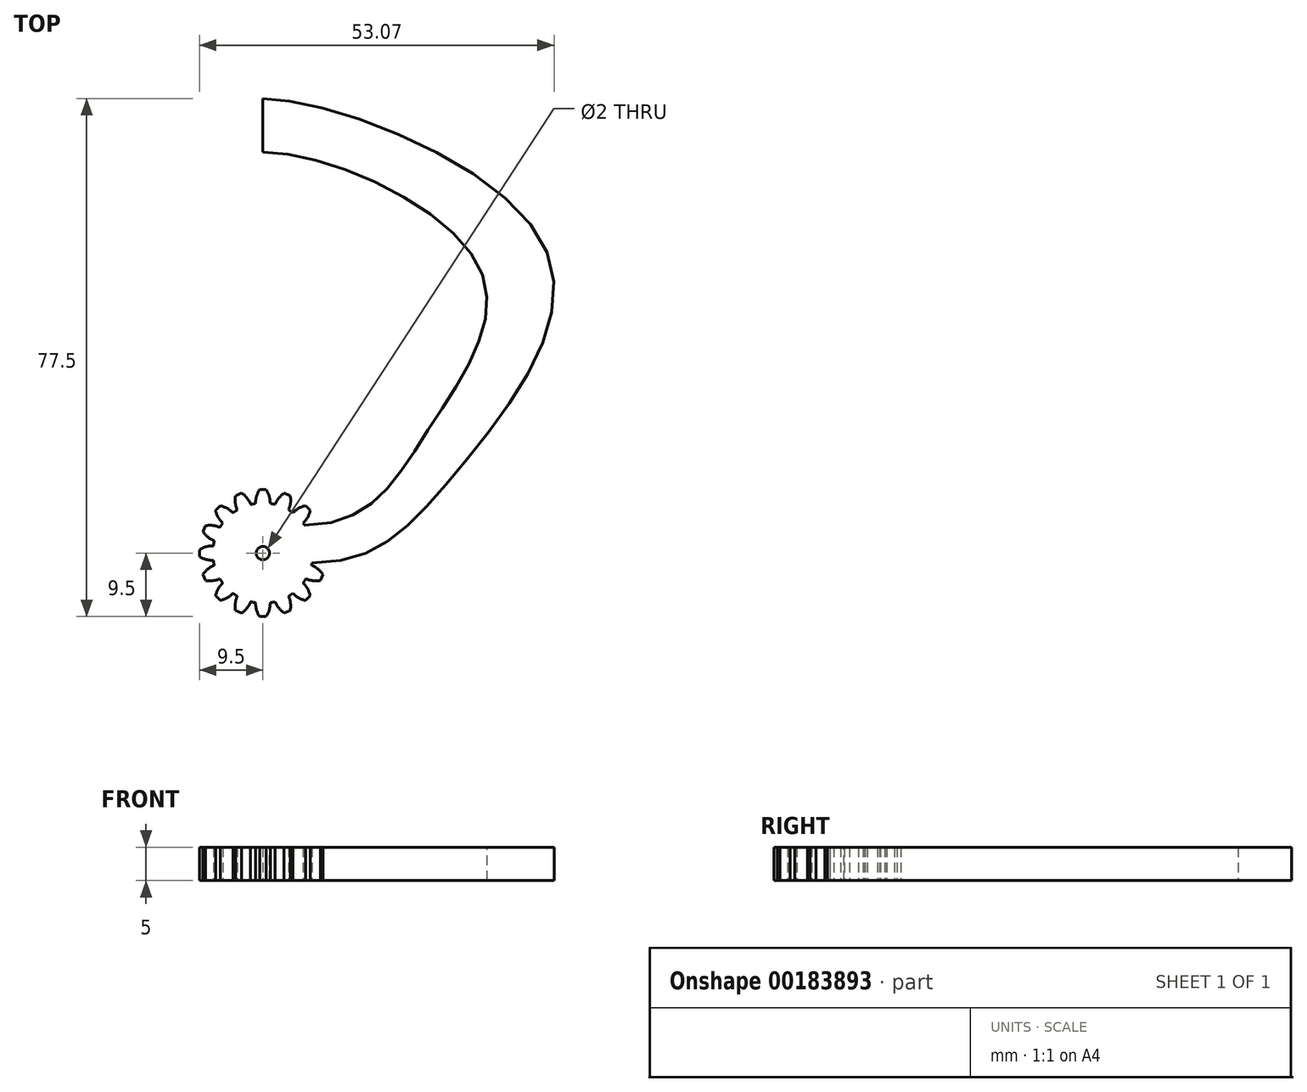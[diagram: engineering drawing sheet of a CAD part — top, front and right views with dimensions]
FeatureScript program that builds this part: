
annotation { "Feature Type Name" : "Feature", "Feature Type Description" : "" }
export const myFeature = defineFeature(function(context is Context, id is Id, definition is map)
    precondition{}
    {
        {
            var Q0;
            Q0=qCreatedBy(makeId("Top.planeOp"),FACE);
            var sketch = newSketch(context, id + "F0", { "sketchPlane" : qUnion([Q0])});
            skCircle(sketch, "E0", {"center": v(0, 0) * mm, "radius": 7.5 * mm});
            skLineSegment(sketch, "E1", {"start": v(0, 0) * mm, "end": v(0, 7.5) * mm, "construction": true});
            skLineSegment(sketch, "E2", {"start": v(0, 9.5) * mm, "end": v(-0.5, 9.5) * mm});
            skArc(sketch, "E3", {"start": v(-0.5, 9.5) * mm, "mid": v(-0.95, 8.5) * mm, "end": v(-1.09, 7.42) * mm});
            skLineSegment(sketch, "E4.MirrorCS", {"start": v(0, 9.5) * mm, "end": v(0.5, 9.5) * mm});
            skArc(sketch, "E5.MirrorCS", {"start": v(0.5, 9.5) * mm, "mid": v(0.95, 8.5) * mm, "end": v(1.09, 7.42) * mm});
            skLineSegment(sketch, "E6.1.0", {"start": v(-3.64, 8.78) * mm, "end": v(-4.1, 8.59) * mm});
            skArc(sketch, "E6.1.1", {"start": v(-4.1, 8.59) * mm, "mid": v(-4.13, 7.5) * mm, "end": v(-3.85, 6.44) * mm});
            skLineSegment(sketch, "E6.1.2", {"start": v(-3.64, 8.78) * mm, "end": v(-3.17, 8.97) * mm});
            skArc(sketch, "E6.1.3", {"start": v(-3.17, 8.97) * mm, "mid": v(-2.38, 8.22) * mm, "end": v(-1.83, 7.27) * mm});
            skLineSegment(sketch, "E6.2.0", {"start": v(-6.72, 6.72) * mm, "end": v(-7.07, 6.36) * mm});
            skArc(sketch, "E6.2.1", {"start": v(-7.07, 6.36) * mm, "mid": v(-6.69, 5.34) * mm, "end": v(-6.02, 4.48) * mm});
            skLineSegment(sketch, "E6.2.2", {"start": v(-6.72, 6.72) * mm, "end": v(-6.36, 7.07) * mm});
            skArc(sketch, "E6.2.3", {"start": v(-6.36, 7.07) * mm, "mid": v(-5.34, 6.69) * mm, "end": v(-4.48, 6.02) * mm});
            skLineSegment(sketch, "E6.3.0", {"start": v(-8.78, 3.64) * mm, "end": v(-8.97, 3.17) * mm});
            skArc(sketch, "E6.3.1", {"start": v(-8.97, 3.17) * mm, "mid": v(-8.22, 2.38) * mm, "end": v(-7.27, 1.83) * mm});
            skLineSegment(sketch, "E6.3.2", {"start": v(-8.78, 3.64) * mm, "end": v(-8.59, 4.1) * mm});
            skArc(sketch, "E6.3.3", {"start": v(-8.59, 4.1) * mm, "mid": v(-7.5, 4.13) * mm, "end": v(-6.44, 3.85) * mm});
            skLineSegment(sketch, "E6.4.0", {"start": v(-9.5, 0) * mm, "end": v(-9.5, -0.5) * mm});
            skArc(sketch, "E6.4.1", {"start": v(-9.5, -0.5) * mm, "mid": v(-8.5, -0.95) * mm, "end": v(-7.42, -1.09) * mm});
            skLineSegment(sketch, "E6.4.2", {"start": v(-9.5, 0) * mm, "end": v(-9.5, 0.5) * mm});
            skArc(sketch, "E6.4.3", {"start": v(-9.5, 0.5) * mm, "mid": v(-8.5, 0.95) * mm, "end": v(-7.42, 1.09) * mm});
            skLineSegment(sketch, "E6.5.0", {"start": v(-8.78, -3.64) * mm, "end": v(-8.59, -4.1) * mm});
            skArc(sketch, "E6.5.1", {"start": v(-8.59, -4.1) * mm, "mid": v(-7.5, -4.13) * mm, "end": v(-6.44, -3.85) * mm});
            skLineSegment(sketch, "E6.5.2", {"start": v(-8.78, -3.64) * mm, "end": v(-8.97, -3.17) * mm});
            skArc(sketch, "E6.5.3", {"start": v(-8.97, -3.17) * mm, "mid": v(-8.22, -2.38) * mm, "end": v(-7.27, -1.83) * mm});
            skLineSegment(sketch, "E6.6.0", {"start": v(-6.72, -6.72) * mm, "end": v(-6.36, -7.07) * mm});
            skArc(sketch, "E6.6.1", {"start": v(-6.36, -7.07) * mm, "mid": v(-5.34, -6.69) * mm, "end": v(-4.48, -6.02) * mm});
            skLineSegment(sketch, "E6.6.2", {"start": v(-6.72, -6.72) * mm, "end": v(-7.07, -6.36) * mm});
            skArc(sketch, "E6.6.3", {"start": v(-7.07, -6.36) * mm, "mid": v(-6.69, -5.34) * mm, "end": v(-6.02, -4.48) * mm});
            skLineSegment(sketch, "E6.7.0", {"start": v(-3.64, -8.78) * mm, "end": v(-3.17, -8.97) * mm});
            skArc(sketch, "E6.7.1", {"start": v(-3.17, -8.97) * mm, "mid": v(-2.38, -8.22) * mm, "end": v(-1.83, -7.27) * mm});
            skLineSegment(sketch, "E6.7.2", {"start": v(-3.64, -8.78) * mm, "end": v(-4.1, -8.59) * mm});
            skArc(sketch, "E6.7.3", {"start": v(-4.1, -8.59) * mm, "mid": v(-4.13, -7.5) * mm, "end": v(-3.85, -6.44) * mm});
            skLineSegment(sketch, "E6.8.0", {"start": v(0, -9.5) * mm, "end": v(0.5, -9.5) * mm});
            skArc(sketch, "E6.8.1", {"start": v(0.5, -9.5) * mm, "mid": v(0.95, -8.5) * mm, "end": v(1.09, -7.42) * mm});
            skLineSegment(sketch, "E6.8.2", {"start": v(0, -9.5) * mm, "end": v(-0.5, -9.5) * mm});
            skArc(sketch, "E6.8.3", {"start": v(-0.5, -9.5) * mm, "mid": v(-0.95, -8.5) * mm, "end": v(-1.09, -7.42) * mm});
            skLineSegment(sketch, "E6.9.0", {"start": v(3.64, -8.78) * mm, "end": v(4.1, -8.59) * mm});
            skArc(sketch, "E6.9.1", {"start": v(4.1, -8.59) * mm, "mid": v(4.13, -7.5) * mm, "end": v(3.85, -6.44) * mm});
            skLineSegment(sketch, "E6.9.2", {"start": v(3.64, -8.78) * mm, "end": v(3.17, -8.97) * mm});
            skArc(sketch, "E6.9.3", {"start": v(3.17, -8.97) * mm, "mid": v(2.38, -8.22) * mm, "end": v(1.83, -7.27) * mm});
            skLineSegment(sketch, "E6.10.0", {"start": v(6.72, -6.72) * mm, "end": v(7.07, -6.36) * mm});
            skArc(sketch, "E6.10.1", {"start": v(7.07, -6.36) * mm, "mid": v(6.69, -5.34) * mm, "end": v(6.02, -4.48) * mm});
            skLineSegment(sketch, "E6.10.2", {"start": v(6.72, -6.72) * mm, "end": v(6.36, -7.07) * mm});
            skArc(sketch, "E6.10.3", {"start": v(6.36, -7.07) * mm, "mid": v(5.34, -6.69) * mm, "end": v(4.48, -6.02) * mm});
            skLineSegment(sketch, "E6.11.0", {"start": v(8.78, -3.64) * mm, "end": v(8.97, -3.17) * mm});
            skArc(sketch, "E6.11.1", {"start": v(8.97, -3.17) * mm, "mid": v(8.22, -2.38) * mm, "end": v(7.27, -1.83) * mm});
            skLineSegment(sketch, "E6.11.2", {"start": v(8.78, -3.64) * mm, "end": v(8.59, -4.1) * mm});
            skArc(sketch, "E6.11.3", {"start": v(8.59, -4.1) * mm, "mid": v(7.5, -4.13) * mm, "end": v(6.44, -3.85) * mm});
            skLineSegment(sketch, "E6.12.0", {"start": v(9.5, 0) * mm, "end": v(9.5, 0.5) * mm});
            skArc(sketch, "E6.12.1", {"start": v(9.5, 0.5) * mm, "mid": v(8.5, 0.95) * mm, "end": v(7.42, 1.09) * mm});
            skLineSegment(sketch, "E6.12.2", {"start": v(9.5, 0) * mm, "end": v(9.5, -0.5) * mm});
            skArc(sketch, "E6.12.3", {"start": v(9.5, -0.5) * mm, "mid": v(8.5, -0.95) * mm, "end": v(7.42, -1.09) * mm});
            skLineSegment(sketch, "E6.13.0", {"start": v(8.78, 3.64) * mm, "end": v(8.59, 4.1) * mm});
            skArc(sketch, "E6.13.1", {"start": v(8.59, 4.1) * mm, "mid": v(7.5, 4.13) * mm, "end": v(6.44, 3.85) * mm});
            skLineSegment(sketch, "E6.13.2", {"start": v(8.78, 3.64) * mm, "end": v(8.97, 3.17) * mm});
            skArc(sketch, "E6.13.3", {"start": v(8.97, 3.17) * mm, "mid": v(8.22, 2.38) * mm, "end": v(7.27, 1.83) * mm});
            skLineSegment(sketch, "E6.14.0", {"start": v(6.72, 6.72) * mm, "end": v(6.36, 7.07) * mm});
            skArc(sketch, "E6.14.1", {"start": v(6.36, 7.07) * mm, "mid": v(5.34, 6.69) * mm, "end": v(4.48, 6.02) * mm});
            skLineSegment(sketch, "E6.14.2", {"start": v(6.72, 6.72) * mm, "end": v(7.07, 6.36) * mm});
            skArc(sketch, "E6.14.3", {"start": v(7.07, 6.36) * mm, "mid": v(6.69, 5.34) * mm, "end": v(6.02, 4.48) * mm});
            skLineSegment(sketch, "E6.15.0", {"start": v(3.64, 8.78) * mm, "end": v(3.17, 8.97) * mm});
            skArc(sketch, "E6.15.1", {"start": v(3.17, 8.97) * mm, "mid": v(2.38, 8.22) * mm, "end": v(1.83, 7.27) * mm});
            skLineSegment(sketch, "E6.15.2", {"start": v(3.64, 8.78) * mm, "end": v(4.1, 8.59) * mm});
            skArc(sketch, "E6.15.3", {"start": v(4.1, 8.59) * mm, "mid": v(4.13, 7.5) * mm, "end": v(3.85, 6.44) * mm});
            skSolve(sketch);
        }
        {
            var Q0;
            Q0=qSketchRegion(id+"F0",true);
            extrude(context, id + "F1", {"entities" : qUnion([Q0]), "depth" : 5 * mm});
        }
        {
            var Q0;
            Q0=makeQuery(id+"F1.opExtrude","CAP_FACE",FACE,{"disambiguationData":[OSD([sQuery(id+"F0.wireOp",EDGE,"E0"),sQuery(id+"F0.wireOp",EDGE,"E2"),sQuery(id+"F0.wireOp",EDGE,"E3"),sQuery(id+"F0.wireOp",EDGE,"E4.MirrorCS"),sQuery(id+"F0.wireOp",EDGE,"E5.MirrorCS"),sQuery(id+"F0.wireOp",EDGE,"E6.1.0"),sQuery(id+"F0.wireOp",EDGE,"E6.1.1"),sQuery(id+"F0.wireOp",EDGE,"E6.1.2"),sQuery(id+"F0.wireOp",EDGE,"E6.1.3"),sQuery(id+"F0.wireOp",EDGE,"E6.2.0"),sQuery(id+"F0.wireOp",EDGE,"E6.2.1"),sQuery(id+"F0.wireOp",EDGE,"E6.2.2"),sQuery(id+"F0.wireOp",EDGE,"E6.2.3"),sQuery(id+"F0.wireOp",EDGE,"E6.3.0"),sQuery(id+"F0.wireOp",EDGE,"E6.3.1"),sQuery(id+"F0.wireOp",EDGE,"E6.3.2"),sQuery(id+"F0.wireOp",EDGE,"E6.3.3"),sQuery(id+"F0.wireOp",EDGE,"E6.4.0"),sQuery(id+"F0.wireOp",EDGE,"E6.4.1"),sQuery(id+"F0.wireOp",EDGE,"E6.4.2"),sQuery(id+"F0.wireOp",EDGE,"E6.4.3"),sQuery(id+"F0.wireOp",EDGE,"E6.5.0"),sQuery(id+"F0.wireOp",EDGE,"E6.5.1"),sQuery(id+"F0.wireOp",EDGE,"E6.5.2"),sQuery(id+"F0.wireOp",EDGE,"E6.5.3"),sQuery(id+"F0.wireOp",EDGE,"E6.6.0"),sQuery(id+"F0.wireOp",EDGE,"E6.6.1"),sQuery(id+"F0.wireOp",EDGE,"E6.6.2"),sQuery(id+"F0.wireOp",EDGE,"E6.6.3"),sQuery(id+"F0.wireOp",EDGE,"E6.7.0"),sQuery(id+"F0.wireOp",EDGE,"E6.7.1"),sQuery(id+"F0.wireOp",EDGE,"E6.7.2"),sQuery(id+"F0.wireOp",EDGE,"E6.7.3"),sQuery(id+"F0.wireOp",EDGE,"E6.8.0"),sQuery(id+"F0.wireOp",EDGE,"E6.8.1"),sQuery(id+"F0.wireOp",EDGE,"E6.8.2"),sQuery(id+"F0.wireOp",EDGE,"E6.8.3"),sQuery(id+"F0.wireOp",EDGE,"E6.9.0"),sQuery(id+"F0.wireOp",EDGE,"E6.9.1"),sQuery(id+"F0.wireOp",EDGE,"E6.9.2"),sQuery(id+"F0.wireOp",EDGE,"E6.9.3"),sQuery(id+"F0.wireOp",EDGE,"E6.10.0"),sQuery(id+"F0.wireOp",EDGE,"E6.10.1"),sQuery(id+"F0.wireOp",EDGE,"E6.10.2"),sQuery(id+"F0.wireOp",EDGE,"E6.10.3"),sQuery(id+"F0.wireOp",EDGE,"E6.11.0"),sQuery(id+"F0.wireOp",EDGE,"E6.11.1"),sQuery(id+"F0.wireOp",EDGE,"E6.11.2"),sQuery(id+"F0.wireOp",EDGE,"E6.11.3"),sQuery(id+"F0.wireOp",EDGE,"E6.12.0"),sQuery(id+"F0.wireOp",EDGE,"E6.12.1"),sQuery(id+"F0.wireOp",EDGE,"E6.12.2"),sQuery(id+"F0.wireOp",EDGE,"E6.12.3"),sQuery(id+"F0.wireOp",EDGE,"E6.13.0"),sQuery(id+"F0.wireOp",EDGE,"E6.13.1"),sQuery(id+"F0.wireOp",EDGE,"E6.13.2"),sQuery(id+"F0.wireOp",EDGE,"E6.13.3"),sQuery(id+"F0.wireOp",EDGE,"E6.14.0"),sQuery(id+"F0.wireOp",EDGE,"E6.14.1"),sQuery(id+"F0.wireOp",EDGE,"E6.14.2"),sQuery(id+"F0.wireOp",EDGE,"E6.14.3"),sQuery(id+"F0.wireOp",EDGE,"E6.15.0"),sQuery(id+"F0.wireOp",EDGE,"E6.15.1"),sQuery(id+"F0.wireOp",EDGE,"E6.15.2"),sQuery(id+"F0.wireOp",EDGE,"E6.15.3")])],"isStart":false});
            var sketch = newSketch(context, id + "F2", { "sketchPlane" : qUnion([Q0])});
            skCircle(sketch, "E7", {"center": v(0, 0) * mm, "radius": 1 * mm});
            skSolve(sketch);
        }
        {
            var Q0;
            Q0=qSketchRegion(id+"F2",true);
            extrude(context, id + "F3", {"entities" : qUnion([Q0]), "operationType" : NewBodyOperationType.REMOVE, "endBound" : BoundingType.THROUGH_ALL, "oppositeDirection" : true, "depth" : 25 * mm});
        }
        {
            var Q0;
            Q0=qCreatedBy(makeId("Top.planeOp"),FACE);
            var sketch = newSketch(context, id + "F4", { "sketchPlane" : qUnion([Q0])});
            skLineSegment(sketch, "E8", {"start": v(0, 68) * mm, "end": v(0, 60) * mm});
            skFitSpline(sketch, "E9", {"points": [v(0, 60) * mm, v(32.58, 42.3) * mm, v(24.56, 18.16) * mm, v(6.24, 4.17) * mm], "startDerivative": vector(78.5, 0) * mm, "endDerivative": vector(-99.55, 0) * mm});
            skFitSpline(sketch, "E10", {"points": [v(0, 68) * mm, v(42.26, 45.66) * mm, v(28.64, 11.75) * mm, v(7.36, -1.46) * mm], "startDerivative": vector(77.95, 0) * mm, "endDerivative": vector(-107.68, 0) * mm});
            skLineSegment(sketch, "E11", {"start": v(6.24, 4.17) * mm, "end": v(7.36, -1.46) * mm});
            skSolve(sketch);
        }
        {
            var Q0;
            Q0 = qSketchRegion(id + "F4", true);
            var Q1;
            Q1=makeQuery(id+"F1.opExtrude","CAP_FACE",FACE,{"disambiguationData":[OSD([sQuery(id+"F0.wireOp",EDGE,"E0"),sQuery(id+"F0.wireOp",EDGE,"E2"),sQuery(id+"F0.wireOp",EDGE,"E3"),sQuery(id+"F0.wireOp",EDGE,"E4.MirrorCS"),sQuery(id+"F0.wireOp",EDGE,"E5.MirrorCS"),sQuery(id+"F0.wireOp",EDGE,"E6.1.0"),sQuery(id+"F0.wireOp",EDGE,"E6.1.1"),sQuery(id+"F0.wireOp",EDGE,"E6.1.2"),sQuery(id+"F0.wireOp",EDGE,"E6.1.3"),sQuery(id+"F0.wireOp",EDGE,"E6.2.0"),sQuery(id+"F0.wireOp",EDGE,"E6.2.1"),sQuery(id+"F0.wireOp",EDGE,"E6.2.2"),sQuery(id+"F0.wireOp",EDGE,"E6.2.3"),sQuery(id+"F0.wireOp",EDGE,"E6.3.0"),sQuery(id+"F0.wireOp",EDGE,"E6.3.1"),sQuery(id+"F0.wireOp",EDGE,"E6.3.2"),sQuery(id+"F0.wireOp",EDGE,"E6.3.3"),sQuery(id+"F0.wireOp",EDGE,"E6.4.0"),sQuery(id+"F0.wireOp",EDGE,"E6.4.1"),sQuery(id+"F0.wireOp",EDGE,"E6.4.2"),sQuery(id+"F0.wireOp",EDGE,"E6.4.3"),sQuery(id+"F0.wireOp",EDGE,"E6.5.0"),sQuery(id+"F0.wireOp",EDGE,"E6.5.1"),sQuery(id+"F0.wireOp",EDGE,"E6.5.2"),sQuery(id+"F0.wireOp",EDGE,"E6.5.3"),sQuery(id+"F0.wireOp",EDGE,"E6.6.0"),sQuery(id+"F0.wireOp",EDGE,"E6.6.1"),sQuery(id+"F0.wireOp",EDGE,"E6.6.2"),sQuery(id+"F0.wireOp",EDGE,"E6.6.3"),sQuery(id+"F0.wireOp",EDGE,"E6.7.0"),sQuery(id+"F0.wireOp",EDGE,"E6.7.1"),sQuery(id+"F0.wireOp",EDGE,"E6.7.2"),sQuery(id+"F0.wireOp",EDGE,"E6.7.3"),sQuery(id+"F0.wireOp",EDGE,"E6.8.0"),sQuery(id+"F0.wireOp",EDGE,"E6.8.1"),sQuery(id+"F0.wireOp",EDGE,"E6.8.2"),sQuery(id+"F0.wireOp",EDGE,"E6.8.3"),sQuery(id+"F0.wireOp",EDGE,"E6.9.0"),sQuery(id+"F0.wireOp",EDGE,"E6.9.1"),sQuery(id+"F0.wireOp",EDGE,"E6.9.2"),sQuery(id+"F0.wireOp",EDGE,"E6.9.3"),sQuery(id+"F0.wireOp",EDGE,"E6.10.0"),sQuery(id+"F0.wireOp",EDGE,"E6.10.1"),sQuery(id+"F0.wireOp",EDGE,"E6.10.2"),sQuery(id+"F0.wireOp",EDGE,"E6.10.3"),sQuery(id+"F0.wireOp",EDGE,"E6.11.0"),sQuery(id+"F0.wireOp",EDGE,"E6.11.1"),sQuery(id+"F0.wireOp",EDGE,"E6.11.2"),sQuery(id+"F0.wireOp",EDGE,"E6.11.3"),sQuery(id+"F0.wireOp",EDGE,"E6.12.0"),sQuery(id+"F0.wireOp",EDGE,"E6.12.1"),sQuery(id+"F0.wireOp",EDGE,"E6.12.2"),sQuery(id+"F0.wireOp",EDGE,"E6.12.3"),sQuery(id+"F0.wireOp",EDGE,"E6.13.0"),sQuery(id+"F0.wireOp",EDGE,"E6.13.1"),sQuery(id+"F0.wireOp",EDGE,"E6.13.2"),sQuery(id+"F0.wireOp",EDGE,"E6.13.3"),sQuery(id+"F0.wireOp",EDGE,"E6.14.0"),sQuery(id+"F0.wireOp",EDGE,"E6.14.1"),sQuery(id+"F0.wireOp",EDGE,"E6.14.2"),sQuery(id+"F0.wireOp",EDGE,"E6.14.3"),sQuery(id+"F0.wireOp",EDGE,"E6.15.0"),sQuery(id+"F0.wireOp",EDGE,"E6.15.1"),sQuery(id+"F0.wireOp",EDGE,"E6.15.2"),sQuery(id+"F0.wireOp",EDGE,"E6.15.3")])],"isStart":false});
            extrude(context, id + "F5", {"entities" : qUnion([Q0]), "operationType" : NewBodyOperationType.ADD, "endBound" : BoundingType.UP_TO_SURFACE, "endBoundEntityFace" : qUnion([Q1]), "depth" : 25 * mm});
        }
    });
